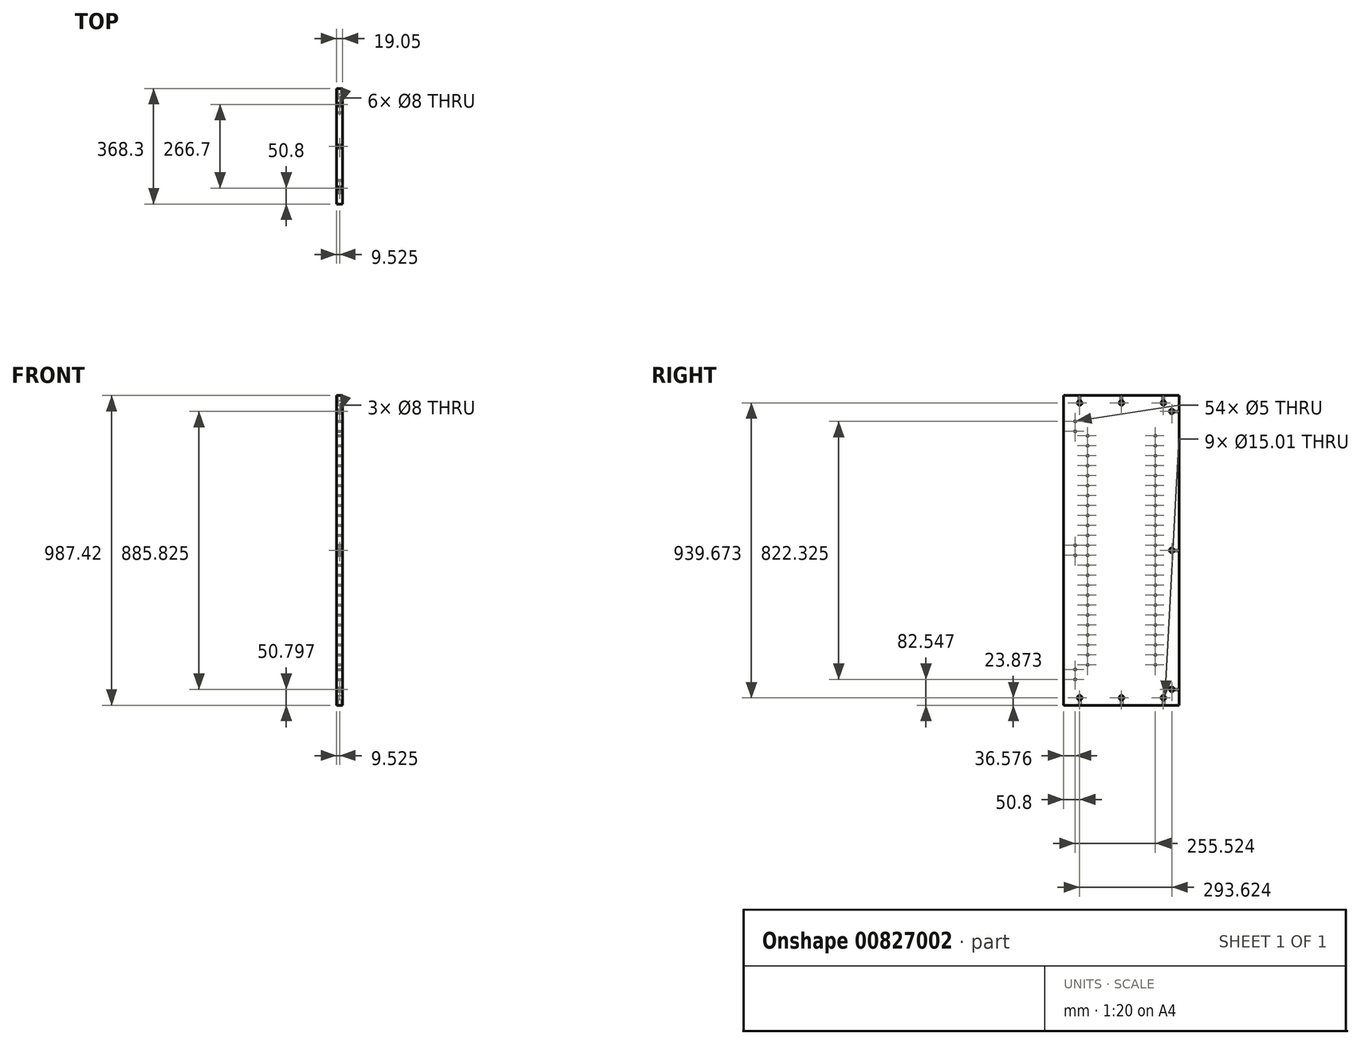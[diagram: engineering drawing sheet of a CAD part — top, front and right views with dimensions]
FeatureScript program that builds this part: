
annotation { "Feature Type Name" : "Feature", "Feature Type Description" : "" }
export const myFeature = defineFeature(function(context is Context, id is Id, definition is map)
    precondition{}
    {
        {
            var Q0;
            Q0=qCreatedBy(makeId("Right.planeOp"),FACE);
            var sketch = newSketch(context, id + "F0", { "sketchPlane" : qUnion([Q0])});
            skLineSegment(sketch, "E0.bottom", {"start": v(184.15, 493.71) * mm, "end": v(-184.15, 493.71) * mm});
            skLineSegment(sketch, "E0.top", {"start": v(184.15, -493.71) * mm, "end": v(-184.15, -493.71) * mm});
            skLineSegment(sketch, "E0.left", {"start": v(184.15, 493.71) * mm, "end": v(184.15, -493.71) * mm});
            skLineSegment(sketch, "E0.right", {"start": v(-184.15, 493.71) * mm, "end": v(-184.15, -493.71) * mm});
            skPoint(sketch, "E0.middle", {"position": v(0, 0) * mm});
            skSolve(sketch);
        }
        {
            var Q0;
            Q0=makeQuery(id+"F0.imprint","IMPRINT",FACE,{"disambiguationData":[TD([[makeQuery(id+"F0.imprint","IMPRINT",EDGE,{"derivedFrom":sQuery(id+"F0.wireOp",EDGE,"E0.bottom")}),1.0]])]});
            extrude(context, id + "F1", {"entities" : qUnion([Q0]), "depth" : 19.05 * mm, "offsetDistance" : 25.4 * mm});
        }
        {
            var Q0;
            Q0=makeQuery(id+"F1.opExtrude","CAP_FACE",FACE,{"disambiguationData":[OSD([sQuery(id+"F0.wireOp",EDGE,"E0.bottom"),sQuery(id+"F0.wireOp",EDGE,"E0.top"),sQuery(id+"F0.wireOp",EDGE,"E0.left"),sQuery(id+"F0.wireOp",EDGE,"E0.right")])],"isStart":false});
            var sketch = newSketch(context, id + "F2", { "sketchPlane" : qUnion([Q0])});
            skLineSegment(sketch, "E1", {"start": v(-184.15, 493.71) * mm, "end": v(-107.95, 493.71) * mm});
            skLineSegment(sketch, "E2", {"start": v(-107.95, 493.71) * mm, "end": v(-107.95, 365.19) * mm});
            skLineSegment(sketch, "E3.bottom", {"start": v(-107.95, 365.19) * mm, "end": v(107.95, 365.19) * mm});
            skLineSegment(sketch, "E3.top", {"start": v(-107.95, 301.69) * mm, "end": v(107.95, 301.69) * mm});
            skLineSegment(sketch, "E3.left", {"start": v(-107.95, 365.19) * mm, "end": v(-107.95, 301.69) * mm});
            skLineSegment(sketch, "E3.right", {"start": v(107.95, 365.19) * mm, "end": v(107.95, 301.69) * mm});
            skLineSegment(sketch, "E4", {"start": v(-107.95, 301.69) * mm, "end": v(-107.95, 269.94) * mm});
            skLineSegment(sketch, "E5.bottom", {"start": v(-107.95, 269.94) * mm, "end": v(107.95, 269.94) * mm});
            skLineSegment(sketch, "E5.top", {"start": v(-107.95, 206.44) * mm, "end": v(107.95, 206.44) * mm});
            skLineSegment(sketch, "E5.left", {"start": v(-107.95, 269.94) * mm, "end": v(-107.95, 206.44) * mm});
            skLineSegment(sketch, "E5.right", {"start": v(107.95, 269.94) * mm, "end": v(107.95, 206.44) * mm});
            skLineSegment(sketch, "E6", {"start": v(-107.95, 206.44) * mm, "end": v(-107.95, 174.69) * mm});
            skLineSegment(sketch, "E7.bottom", {"start": v(-107.95, 174.69) * mm, "end": v(107.95, 174.69) * mm});
            skLineSegment(sketch, "E7.top", {"start": v(-107.95, 111.19) * mm, "end": v(107.95, 111.19) * mm});
            skLineSegment(sketch, "E7.left", {"start": v(-107.95, 174.69) * mm, "end": v(-107.95, 111.19) * mm});
            skLineSegment(sketch, "E7.right", {"start": v(107.95, 174.69) * mm, "end": v(107.95, 111.19) * mm});
            skLineSegment(sketch, "E8", {"start": v(-107.95, 111.19) * mm, "end": v(-107.95, 79.44) * mm});
            skLineSegment(sketch, "E9.bottom", {"start": v(-107.95, 79.44) * mm, "end": v(107.95, 79.44) * mm});
            skLineSegment(sketch, "E9.top", {"start": v(-107.95, 15.94) * mm, "end": v(107.95, 15.94) * mm});
            skLineSegment(sketch, "E9.left", {"start": v(-107.95, 79.44) * mm, "end": v(-107.95, 15.94) * mm});
            skLineSegment(sketch, "E9.right", {"start": v(107.95, 79.44) * mm, "end": v(107.95, 15.94) * mm});
            skLineSegment(sketch, "E10", {"start": v(-107.95, 15.94) * mm, "end": v(-107.95, -15.81) * mm});
            skLineSegment(sketch, "E11.bottom", {"start": v(-107.95, -15.81) * mm, "end": v(107.95, -15.81) * mm});
            skLineSegment(sketch, "E11.top", {"start": v(-107.95, -79.31) * mm, "end": v(107.95, -79.31) * mm});
            skLineSegment(sketch, "E11.left", {"start": v(-107.95, -15.81) * mm, "end": v(-107.95, -79.31) * mm});
            skLineSegment(sketch, "E11.right", {"start": v(107.95, -15.81) * mm, "end": v(107.95, -79.31) * mm});
            skLineSegment(sketch, "E12", {"start": v(-107.95, -79.31) * mm, "end": v(-107.95, -111.06) * mm});
            skLineSegment(sketch, "E13.bottom", {"start": v(-107.95, -111.06) * mm, "end": v(107.95, -111.06) * mm});
            skLineSegment(sketch, "E13.top", {"start": v(-107.95, -174.56) * mm, "end": v(107.95, -174.56) * mm});
            skLineSegment(sketch, "E13.left", {"start": v(-107.95, -111.06) * mm, "end": v(-107.95, -174.56) * mm});
            skLineSegment(sketch, "E13.right", {"start": v(107.95, -111.06) * mm, "end": v(107.95, -174.56) * mm});
            skLineSegment(sketch, "E14", {"start": v(-107.95, -174.56) * mm, "end": v(-107.95, -206.31) * mm});
            skLineSegment(sketch, "E15.bottom", {"start": v(-107.95, -206.31) * mm, "end": v(107.95, -206.31) * mm});
            skLineSegment(sketch, "E15.top", {"start": v(-107.95, -269.81) * mm, "end": v(107.95, -269.81) * mm});
            skLineSegment(sketch, "E15.left", {"start": v(-107.95, -206.31) * mm, "end": v(-107.95, -269.81) * mm});
            skLineSegment(sketch, "E15.right", {"start": v(107.95, -206.31) * mm, "end": v(107.95, -269.81) * mm});
            skLineSegment(sketch, "E16", {"start": v(-107.95, -269.81) * mm, "end": v(-107.95, -301.56) * mm});
            skLineSegment(sketch, "E17.bottom", {"start": v(-107.95, -301.56) * mm, "end": v(107.95, -301.56) * mm});
            skLineSegment(sketch, "E17.top", {"start": v(-107.95, -365.06) * mm, "end": v(107.95, -365.06) * mm});
            skLineSegment(sketch, "E17.left", {"start": v(-107.95, -301.56) * mm, "end": v(-107.95, -365.06) * mm});
            skLineSegment(sketch, "E17.right", {"start": v(107.95, -301.56) * mm, "end": v(107.95, -365.06) * mm});
            skLineSegment(sketch, "E18", {"start": v(-184.15, 493.71) * mm, "end": v(-184.15, 411.16) * mm});
            skLineSegment(sketch, "E19", {"start": v(-184.15, 411.16) * mm, "end": v(-147.57, 411.16) * mm});
            skLineSegment(sketch, "E20", {"start": v(-147.57, 411.16) * mm, "end": v(-147.57, 379.41) * mm});
            skLineSegment(sketch, "E21", {"start": v(-184.15, -493.71) * mm, "end": v(-184.15, -411.16) * mm});
            skLineSegment(sketch, "E22", {"start": v(-184.15, -411.16) * mm, "end": v(-147.57, -411.16) * mm});
            skLineSegment(sketch, "E23", {"start": v(-147.57, -411.16) * mm, "end": v(-147.57, -379.41) * mm});
            skLineSegment(sketch, "E24", {"start": v(-184.15, 0) * mm, "end": v(-147.57, 0) * mm});
            skLineSegment(sketch, "E25", {"start": v(-147.57, 0) * mm, "end": v(-147.57, -15.88) * mm});
            skLineSegment(sketch, "E26", {"start": v(-147.57, 0) * mm, "end": v(-147.57, 15.88) * mm});
            skPoint(sketch, "E27", {"position": v(-147.57, 411.16) * mm});
            skPoint(sketch, "E28", {"position": v(-147.57, 379.41) * mm});
            skPoint(sketch, "E29", {"position": v(-147.57, 15.88) * mm});
            skPoint(sketch, "E30", {"position": v(-147.57, -15.88) * mm});
            skPoint(sketch, "E31", {"position": v(-147.57, -379.41) * mm});
            skPoint(sketch, "E32", {"position": v(-147.57, -411.16) * mm});
            skPoint(sketch, "E33", {"position": v(-107.95, 365.19) * mm});
            skPoint(sketch, "E34", {"position": v(-107.95, 333.44) * mm});
            skPoint(sketch, "E35", {"position": v(-107.95, 301.69) * mm});
            skPoint(sketch, "E36", {"position": v(-107.95, 269.94) * mm});
            skPoint(sketch, "E37", {"position": v(-107.95, 238.19) * mm});
            skPoint(sketch, "E38", {"position": v(-107.95, 206.44) * mm});
            skPoint(sketch, "E39", {"position": v(-107.95, 174.69) * mm});
            skPoint(sketch, "E40", {"position": v(-107.95, 142.94) * mm});
            skPoint(sketch, "E41", {"position": v(-107.95, 79.44) * mm});
            skPoint(sketch, "E42", {"position": v(-107.95, 47.69) * mm});
            skPoint(sketch, "E43", {"position": v(-107.95, 15.94) * mm});
            skPoint(sketch, "E44", {"position": v(-107.95, -15.81) * mm});
            skPoint(sketch, "E45", {"position": v(-107.95, -47.56) * mm});
            skPoint(sketch, "E46", {"position": v(-107.95, -79.31) * mm});
            skPoint(sketch, "E47", {"position": v(-107.95, -111.06) * mm});
            skPoint(sketch, "E48", {"position": v(-107.95, -142.81) * mm});
            skPoint(sketch, "E49", {"position": v(-107.95, -174.56) * mm});
            skPoint(sketch, "E50", {"position": v(-107.95, -206.31) * mm});
            skPoint(sketch, "E51", {"position": v(-107.95, -238.06) * mm});
            skPoint(sketch, "E52", {"position": v(-107.95, -269.81) * mm});
            skPoint(sketch, "E53", {"position": v(-107.95, -301.56) * mm});
            skPoint(sketch, "E54", {"position": v(-107.95, -333.31) * mm});
            skPoint(sketch, "E55", {"position": v(-107.95, -365.06) * mm});
            skPoint(sketch, "E56", {"position": v(107.95, -365.06) * mm});
            skPoint(sketch, "E57", {"position": v(107.95, -333.31) * mm});
            skPoint(sketch, "E58", {"position": v(107.95, -301.56) * mm});
            skPoint(sketch, "E59", {"position": v(107.95, -269.81) * mm});
            skPoint(sketch, "E60", {"position": v(107.95, -238.06) * mm});
            skPoint(sketch, "E61", {"position": v(107.95, -206.31) * mm});
            skPoint(sketch, "E62", {"position": v(107.95, -174.56) * mm});
            skPoint(sketch, "E63", {"position": v(107.95, -142.81) * mm});
            skPoint(sketch, "E64", {"position": v(107.95, -111.06) * mm});
            skPoint(sketch, "E65", {"position": v(107.95, -79.31) * mm});
            skPoint(sketch, "E66", {"position": v(107.95, -47.56) * mm});
            skPoint(sketch, "E67", {"position": v(107.95, -15.81) * mm});
            skPoint(sketch, "E68", {"position": v(107.95, 15.94) * mm});
            skPoint(sketch, "E69", {"position": v(107.95, 47.69) * mm});
            skPoint(sketch, "E70", {"position": v(107.95, 79.44) * mm});
            skPoint(sketch, "E71", {"position": v(107.95, 111.19) * mm});
            skPoint(sketch, "E72", {"position": v(107.95, 142.94) * mm});
            skPoint(sketch, "E73", {"position": v(107.95, 174.69) * mm});
            skPoint(sketch, "E74", {"position": v(107.95, 238.19) * mm});
            skPoint(sketch, "E75", {"position": v(107.95, 206.44) * mm});
            skPoint(sketch, "E76", {"position": v(107.95, 269.94) * mm});
            skPoint(sketch, "E77", {"position": v(107.95, 301.69) * mm});
            skPoint(sketch, "E78", {"position": v(107.95, 333.44) * mm});
            skPoint(sketch, "E79", {"position": v(107.95, 365.19) * mm});
            skSolve(sketch);
        }
        {
            var Q0;
            Q0=sQuery(id+"F2.wireOp",VERTEX,"E33");
            var Q1;
            Q1=sQuery(id+"F2.wireOp",VERTEX,"E35");
            var Q2;
            Q2=sQuery(id+"F2.wireOp",VERTEX,"E36");
            var Q3;
            Q3=sQuery(id+"F2.wireOp",VERTEX,"E38");
            var Q4;
            Q4=sQuery(id+"F2.wireOp",VERTEX,"E39");
            var Q5;
            Q5=sQuery(id+"F2.wireOp",VERTEX,"E7.top.start");
            var Q6;
            Q6=sQuery(id+"F2.wireOp",VERTEX,"E41");
            var Q7;
            Q7=sQuery(id+"F2.wireOp",VERTEX,"E43");
            var Q8;
            Q8=sQuery(id+"F2.wireOp",VERTEX,"E44");
            var Q9;
            Q9=sQuery(id+"F2.wireOp",VERTEX,"E45");
            var Q10;
            Q10=sQuery(id+"F2.wireOp",VERTEX,"E46");
            var Q11;
            Q11=sQuery(id+"F2.wireOp",VERTEX,"E47");
            var Q12;
            Q12=sQuery(id+"F2.wireOp",VERTEX,"E49");
            var Q13;
            Q13=sQuery(id+"F2.wireOp",VERTEX,"E50");
            var Q14;
            Q14=sQuery(id+"F2.wireOp",VERTEX,"E52");
            var Q15;
            Q15=sQuery(id+"F2.wireOp",VERTEX,"E53");
            var Q16;
            Q16=sQuery(id+"F2.wireOp",VERTEX,"E54");
            var Q17;
            Q17=sQuery(id+"F2.wireOp",VERTEX,"E55");
            var Q18;
            Q18=sQuery(id+"F2.wireOp",VERTEX,"E56");
            var Q19;
            Q19=sQuery(id+"F2.wireOp",VERTEX,"E58");
            var Q20;
            Q20=sQuery(id+"F2.wireOp",VERTEX,"E59");
            var Q21;
            Q21=sQuery(id+"F2.wireOp",VERTEX,"E61");
            var Q22;
            Q22=sQuery(id+"F2.wireOp",VERTEX,"E62");
            var Q23;
            Q23=sQuery(id+"F2.wireOp",VERTEX,"E64");
            var Q24;
            Q24=sQuery(id+"F2.wireOp",VERTEX,"E65");
            var Q25;
            Q25=sQuery(id+"F2.wireOp",VERTEX,"E67");
            var Q26;
            Q26=sQuery(id+"F2.wireOp",VERTEX,"E68");
            var Q27;
            Q27=sQuery(id+"F2.wireOp",VERTEX,"E70");
            var Q28;
            Q28=sQuery(id+"F2.wireOp",VERTEX,"E71");
            var Q29;
            Q29=sQuery(id+"F2.wireOp",VERTEX,"E73");
            var Q30;
            Q30=sQuery(id+"F2.wireOp",VERTEX,"E75");
            var Q31;
            Q31=sQuery(id+"F2.wireOp",VERTEX,"E74");
            var Q32;
            Q32=sQuery(id+"F2.wireOp",VERTEX,"E76");
            var Q33;
            Q33=sQuery(id+"F2.wireOp",VERTEX,"E77");
            var Q34;
            Q34=sQuery(id+"F2.wireOp",VERTEX,"E79");
            var Q35;
            Q35=sQuery(id+"F2.wireOp",VERTEX,"E34");
            var Q36;
            Q36=sQuery(id+"F2.wireOp",VERTEX,"E78");
            var Q37;
            Q37=sQuery(id+"F2.wireOp",VERTEX,"E37");
            var Q38;
            Q38=sQuery(id+"F2.wireOp",VERTEX,"E40");
            var Q39;
            Q39=sQuery(id+"F2.wireOp",VERTEX,"E72");
            var Q40;
            Q40=sQuery(id+"F2.wireOp",VERTEX,"E69");
            var Q41;
            Q41=sQuery(id+"F2.wireOp",VERTEX,"E42");
            var Q42;
            Q42=sQuery(id+"F2.wireOp",VERTEX,"E66");
            var Q43;
            Q43=sQuery(id+"F2.wireOp",VERTEX,"E63");
            var Q44;
            Q44=sQuery(id+"F2.wireOp",VERTEX,"E48");
            var Q45;
            Q45=sQuery(id+"F2.wireOp",VERTEX,"E51");
            var Q46;
            Q46=sQuery(id+"F2.wireOp",VERTEX,"E60");
            var Q47;
            Q47=sQuery(id+"F2.wireOp",VERTEX,"E57");
            var Q48;
            Q48=makeQuery(id+"F1.opExtrude","SWEPT_BODY",BODY,{"disambiguationData":[OSD([sQuery(id+"F0.wireOp",EDGE,"E0.bottom"),sQuery(id+"F0.wireOp",EDGE,"E0.top"),sQuery(id+"F0.wireOp",EDGE,"E0.left"),sQuery(id+"F0.wireOp",EDGE,"E0.right")])]});
            hole(context, id + "F3", {"style" : HoleStyle.SIMPLE, "endStyle" : HoleEndStyle.BLIND, "holeDiameter" : 5 * mm, "majorDiameter" : 6.35 * mm, "holeDepth" : 25.4 * mm, "isTappedThrough" : true, "tappedDepth" : 12.7 * mm, "tapClearance" : 3, "startFromSketch" : true, "locations" : qUnion([Q0, Q1, Q2, Q3, Q4, Q5, Q6, Q7, Q8, Q9, Q10, Q11, Q12, Q13, Q14, Q15, Q16, Q17, Q18, Q19, Q20, Q21, Q22, Q23, Q24, Q25, Q26, Q27, Q28, Q29, Q30, Q31, Q32, Q33, Q34, Q35, Q36, Q37, Q38, Q39, Q40, Q41, Q42, Q43, Q44, Q45, Q46, Q47]), "scope" : qUnion([Q48])});
        }
        {
            var Q0;
            Q0=makeQuery(id+"F1.opExtrude","CAP_FACE",FACE,{"disambiguationData":[OSD([sQuery(id+"F0.wireOp",EDGE,"E0.bottom"),sQuery(id+"F0.wireOp",EDGE,"E0.top"),sQuery(id+"F0.wireOp",EDGE,"E0.left"),sQuery(id+"F0.wireOp",EDGE,"E0.right")])],"isStart":false});
            var sketch = newSketch(context, id + "F4", { "sketchPlane" : qUnion([Q0])});
            skLineSegment(sketch, "E80", {"start": v(-184.15, 493.71) * mm, "end": v(-133.35, 493.71) * mm});
            skLineSegment(sketch, "E81", {"start": v(-133.35, 493.71) * mm, "end": v(-133.35, 469.84) * mm});
            skLineSegment(sketch, "E82", {"start": v(184.15, 493.71) * mm, "end": v(133.35, 493.71) * mm});
            skLineSegment(sketch, "E83", {"start": v(133.35, 493.71) * mm, "end": v(133.35, 469.84) * mm});
            skLineSegment(sketch, "E84", {"start": v(0, 493.71) * mm, "end": v(0, 469.84) * mm});
            skPoint(sketch, "E85", {"position": v(133.35, 469.84) * mm});
            skPoint(sketch, "E86", {"position": v(0, 469.84) * mm});
            skPoint(sketch, "E87", {"position": v(-133.35, 469.84) * mm});
            skLineSegment(sketch, "E88", {"start": v(-184.15, -493.71) * mm, "end": v(-133.35, -493.71) * mm});
            skLineSegment(sketch, "E89", {"start": v(-133.35, -493.71) * mm, "end": v(-133.35, -469.84) * mm});
            skLineSegment(sketch, "E90", {"start": v(184.15, -493.71) * mm, "end": v(133.35, -493.71) * mm});
            skLineSegment(sketch, "E91", {"start": v(133.35, -493.71) * mm, "end": v(133.35, -469.84) * mm});
            skLineSegment(sketch, "E92", {"start": v(0, -493.71) * mm, "end": v(0, -469.84) * mm});
            skPoint(sketch, "E93", {"position": v(-133.35, -469.84) * mm});
            skPoint(sketch, "E94", {"position": v(0, -469.84) * mm});
            skPoint(sketch, "E95", {"position": v(133.35, -469.84) * mm});
            skSolve(sketch);
        }
        {
            var Q0;
            Q0=sQuery(id+"F4.wireOp",VERTEX,"E93");
            var Q1;
            Q1=sQuery(id+"F4.wireOp",VERTEX,"E94");
            var Q2;
            Q2=sQuery(id+"F4.wireOp",VERTEX,"E95");
            var Q3;
            Q3=sQuery(id+"F4.wireOp",VERTEX,"E87");
            var Q4;
            Q4=sQuery(id+"F4.wireOp",VERTEX,"E86");
            var Q5;
            Q5=sQuery(id+"F4.wireOp",VERTEX,"E85");
            var Q6;
            Q6=makeQuery(id+"F1.opExtrude","SWEPT_BODY",BODY,{"disambiguationData":[OSD([sQuery(id+"F0.wireOp",EDGE,"E0.bottom"),sQuery(id+"F0.wireOp",EDGE,"E0.top"),sQuery(id+"F0.wireOp",EDGE,"E0.left"),sQuery(id+"F0.wireOp",EDGE,"E0.right")])]});
            hole(context, id + "F5", {"style" : HoleStyle.SIMPLE, "endStyle" : HoleEndStyle.BLIND, "holeDiameter" : 15 * mm, "majorDiameter" : 6.35 * mm, "holeDepth" : 14.22 * mm, "isTappedThrough" : true, "tappedDepth" : 12.7 * mm, "tapClearance" : 3, "startFromSketch" : true, "locations" : qUnion([Q0, Q1, Q2, Q3, Q4, Q5]), "scope" : qUnion([Q6])});
        }
        {
            var Q0;
            Q0=sQuery(id+"F2.wireOp",VERTEX,"E27");
            var Q1;
            Q1=sQuery(id+"F2.wireOp",VERTEX,"E28");
            var Q2;
            Q2=sQuery(id+"F2.wireOp",VERTEX,"E29");
            var Q3;
            Q3=sQuery(id+"F2.wireOp",VERTEX,"E30");
            var Q4;
            Q4=sQuery(id+"F2.wireOp",VERTEX,"E31");
            var Q5;
            Q5=sQuery(id+"F2.wireOp",VERTEX,"E32");
            var Q6;
            Q6=makeQuery(id+"F1.opExtrude","SWEPT_BODY",BODY,{"disambiguationData":[OSD([sQuery(id+"F0.wireOp",EDGE,"E0.bottom"),sQuery(id+"F0.wireOp",EDGE,"E0.top"),sQuery(id+"F0.wireOp",EDGE,"E0.left"),sQuery(id+"F0.wireOp",EDGE,"E0.right")])]});
            hole(context, id + "F6", {"style" : HoleStyle.SIMPLE, "endStyle" : HoleEndStyle.BLIND, "holeDiameter" : 5 * mm, "majorDiameter" : 6.35 * mm, "holeDepth" : 14.22 * mm, "isTappedThrough" : true, "tappedDepth" : 12.7 * mm, "tapClearance" : 3, "startFromSketch" : true, "locations" : qUnion([Q0, Q1, Q2, Q3, Q4, Q5]), "scope" : qUnion([Q6])});
        }
        {
            var Q0;
            Q0=makeQuery(id+"F1.opExtrude","CAP_FACE",FACE,{"disambiguationData":[OSD([sQuery(id+"F0.wireOp",EDGE,"E0.bottom"),sQuery(id+"F0.wireOp",EDGE,"E0.top"),sQuery(id+"F0.wireOp",EDGE,"E0.left"),sQuery(id+"F0.wireOp",EDGE,"E0.right")])],"isStart":false});
            var sketch = newSketch(context, id + "F7", { "sketchPlane" : qUnion([Q0])});
            skLineSegment(sketch, "E96", {"start": v(184.15, 493.71) * mm, "end": v(160.27, 493.71) * mm});
            skLineSegment(sketch, "E97", {"start": v(160.27, 493.71) * mm, "end": v(160.27, 442.91) * mm});
            skLineSegment(sketch, "E98", {"start": v(184.15, -493.71) * mm, "end": v(160.27, -493.71) * mm});
            skLineSegment(sketch, "E99", {"start": v(160.27, -493.71) * mm, "end": v(160.27, -442.91) * mm});
            skLineSegment(sketch, "E100", {"start": v(184.15, 0) * mm, "end": v(160.27, 0) * mm});
            skSolve(sketch);
        }
        {
            var Q0;
            Q0=sQuery(id+"F7.wireOp",VERTEX,"E97.end");
            var Q1;
            Q1=sQuery(id+"F7.wireOp",VERTEX,"E100.end");
            var Q2;
            Q2=sQuery(id+"F7.wireOp",VERTEX,"E99.end");
            var Q3;
            Q3=makeQuery(id+"F1.opExtrude","SWEPT_BODY",BODY,{"disambiguationData":[OSD([sQuery(id+"F0.wireOp",EDGE,"E0.bottom"),sQuery(id+"F0.wireOp",EDGE,"E0.top"),sQuery(id+"F0.wireOp",EDGE,"E0.left"),sQuery(id+"F0.wireOp",EDGE,"E0.right")])]});
            hole(context, id + "F8", {"style" : HoleStyle.SIMPLE, "endStyle" : HoleEndStyle.BLIND, "holeDiameter" : 15 * mm, "majorDiameter" : 6.35 * mm, "holeDepth" : 14.22 * mm, "isTappedThrough" : true, "tappedDepth" : 12.7 * mm, "tapClearance" : 3, "startFromSketch" : true, "locations" : qUnion([Q0, Q1, Q2]), "scope" : qUnion([Q3])});
        }
        {
            var Q0;
            Q0=makeQuery(id+"F1.opExtrude","SWEPT_FACE",FACE,{"disambiguationData":[OSD([sQuery(id+"F0.wireOp",EDGE,"E0.top")])]});
            var sketch = newSketch(context, id + "F9", { "sketchPlane" : qUnion([Q0])});
            skLineSegment(sketch, "E101", {"start": v(9.53, 184.15) * mm, "end": v(9.53, 133.35) * mm});
            skLineSegment(sketch, "E102", {"start": v(9.53, -184.15) * mm, "end": v(9.53, -133.35) * mm});
            skLineSegment(sketch, "E103", {"start": v(0, 0) * mm, "end": v(9.53, 0) * mm});
            skPoint(sketch, "E104", {"position": v(9.53, 133.35) * mm});
            skPoint(sketch, "E105", {"position": v(9.53, 0) * mm});
            skPoint(sketch, "E106", {"position": v(9.53, -133.35) * mm});
            skSolve(sketch);
        }
        {
            var Q0;
            Q0=sQuery(id+"F9.wireOp",VERTEX,"E104");
            var Q1;
            Q1=sQuery(id+"F9.wireOp",VERTEX,"E105");
            var Q2;
            Q2=sQuery(id+"F9.wireOp",VERTEX,"E106");
            var Q3;
            Q3=makeQuery(id+"F1.opExtrude","SWEPT_BODY",BODY,{"disambiguationData":[OSD([sQuery(id+"F0.wireOp",EDGE,"E0.bottom"),sQuery(id+"F0.wireOp",EDGE,"E0.top"),sQuery(id+"F0.wireOp",EDGE,"E0.left"),sQuery(id+"F0.wireOp",EDGE,"E0.right")])]});
            hole(context, id + "F10", {"style" : HoleStyle.SIMPLE, "endStyle" : HoleEndStyle.BLIND, "holeDiameter" : 8 * mm, "majorDiameter" : 6.35 * mm, "holeDepth" : 25.4 * mm, "isTappedThrough" : true, "tappedDepth" : 12.7 * mm, "tapClearance" : 3, "startFromSketch" : true, "locations" : qUnion([Q0, Q1, Q2]), "scope" : qUnion([Q3])});
        }
        {
            var Q0;
            Q0=makeQuery(id+"F1.opExtrude","SWEPT_FACE",FACE,{"disambiguationData":[OSD([sQuery(id+"F0.wireOp",EDGE,"E0.bottom")])]});
            var sketch = newSketch(context, id + "F11", { "sketchPlane" : qUnion([Q0])});
            skLineSegment(sketch, "E107", {"start": v(9.53, 184.15) * mm, "end": v(9.53, 133.35) * mm});
            skLineSegment(sketch, "E108", {"start": v(9.53, -184.15) * mm, "end": v(9.53, -133.35) * mm});
            skLineSegment(sketch, "E109", {"start": v(0, 0) * mm, "end": v(9.53, 0) * mm});
            skPoint(sketch, "E110", {"position": v(9.53, 133.35) * mm});
            skPoint(sketch, "E111", {"position": v(9.53, 0) * mm});
            skPoint(sketch, "E112", {"position": v(9.53, -133.35) * mm});
            skSolve(sketch);
        }
        {
            var Q0;
            Q0=sQuery(id+"F11.wireOp",VERTEX,"E110");
            var Q1;
            Q1=sQuery(id+"F11.wireOp",VERTEX,"E111");
            var Q2;
            Q2=sQuery(id+"F11.wireOp",VERTEX,"E112");
            var Q3;
            Q3=makeQuery(id+"F1.opExtrude","SWEPT_BODY",BODY,{"disambiguationData":[OSD([sQuery(id+"F0.wireOp",EDGE,"E0.bottom"),sQuery(id+"F0.wireOp",EDGE,"E0.top"),sQuery(id+"F0.wireOp",EDGE,"E0.left"),sQuery(id+"F0.wireOp",EDGE,"E0.right")])]});
            hole(context, id + "F12", {"style" : HoleStyle.SIMPLE, "endStyle" : HoleEndStyle.BLIND, "holeDiameter" : 8 * mm, "majorDiameter" : 6.35 * mm, "holeDepth" : 25.4 * mm, "isTappedThrough" : true, "tappedDepth" : 12.7 * mm, "tapClearance" : 3, "startFromSketch" : true, "locations" : qUnion([Q0, Q1, Q2]), "scope" : qUnion([Q3])});
        }
        {
            var Q0;
            Q0=makeQuery(id+"F1.opExtrude","SWEPT_FACE",FACE,{"disambiguationData":[OSD([sQuery(id+"F0.wireOp",EDGE,"E0.left")])]});
            var sketch = newSketch(context, id + "F13", { "sketchPlane" : qUnion([Q0])});
            skLineSegment(sketch, "E113", {"start": v(-9.53, 493.71) * mm, "end": v(-9.53, 442.91) * mm});
            skLineSegment(sketch, "E114", {"start": v(-9.53, -493.71) * mm, "end": v(-9.53, -442.91) * mm});
            skLineSegment(sketch, "E115", {"start": v(0, 0) * mm, "end": v(-9.53, 0) * mm});
            skSolve(sketch);
        }
        {
            var Q0;
            Q0=sQuery(id+"F13.wireOp",VERTEX,"E114.end");
            var Q1;
            Q1=sQuery(id+"F13.wireOp",VERTEX,"E115.end");
            var Q2;
            Q2=sQuery(id+"F13.wireOp",VERTEX,"E113.end");
            var Q3;
            Q3=makeQuery(id+"F1.opExtrude","SWEPT_BODY",BODY,{"disambiguationData":[OSD([sQuery(id+"F0.wireOp",EDGE,"E0.bottom"),sQuery(id+"F0.wireOp",EDGE,"E0.top"),sQuery(id+"F0.wireOp",EDGE,"E0.left"),sQuery(id+"F0.wireOp",EDGE,"E0.right")])]});
            hole(context, id + "F14", {"style" : HoleStyle.SIMPLE, "endStyle" : HoleEndStyle.BLIND, "holeDiameter" : 8 * mm, "majorDiameter" : 6.35 * mm, "holeDepth" : 25.4 * mm, "isTappedThrough" : true, "tappedDepth" : 12.7 * mm, "tapClearance" : 3, "startFromSketch" : true, "locations" : qUnion([Q0, Q1, Q2]), "scope" : qUnion([Q3])});
        }
    });
